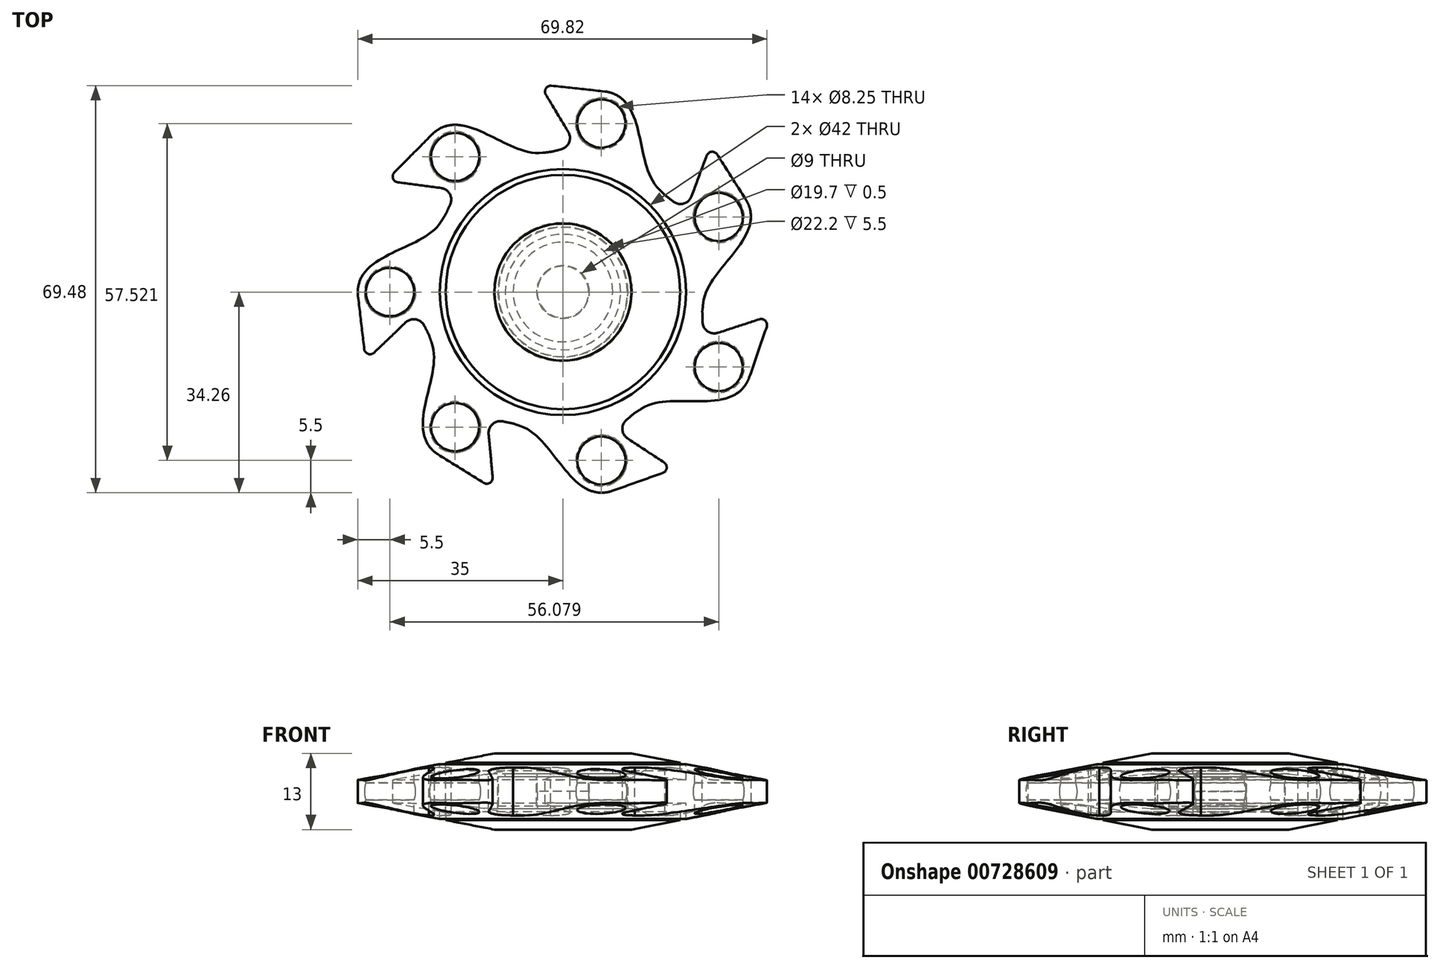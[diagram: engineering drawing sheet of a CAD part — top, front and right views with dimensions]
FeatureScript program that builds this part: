
annotation { "Feature Type Name" : "Feature", "Feature Type Description" : "" }
export const myFeature = defineFeature(function(context is Context, id is Id, definition is map)
    precondition{}
    {
        {
            var Q0;
            Q0=qCreatedBy(makeId("Front.planeOp"),FACE);
            var sketch = newSketch(context, id + "F0", { "sketchPlane" : qUnion([Q0])});
            skLineSegment(sketch, "E0.right", {"start": v(-4.5, -2.5) * mm, "end": v(-4.5, 2.5) * mm});
            skPoint(sketch, "E0.middle", {"position": v(0, 0) * mm});
            skLineSegment(sketch, "E1.right", {"start": v(-20, 6.5) * mm, "end": v(-20, 3.5) * mm});
            skLineSegment(sketch, "E2.right", {"start": v(-8.5, 3) * mm, "end": v(-8.5, 3.5) * mm});
            skLineSegment(sketch, "E3", {"start": v(-8.5, 3.5) * mm, "end": v(-20, 3.5) * mm});
            skLineSegment(sketch, "E4", {"start": v(-11, 2.5) * mm, "end": v(-11, -2.5) * mm});
            skLineSegment(sketch, "E5.top", {"start": v(-4.4, 0) * mm, "end": v(0, 0) * mm});
            skLineSegment(sketch, "E5.left", {"start": v(-4.4, 3) * mm, "end": v(-4.4, 0) * mm});
            skLineSegment(sketch, "E6", {"start": v(-8.5, 3) * mm, "end": v(-4.4, 3) * mm});
            skLineSegment(sketch, "E7", {"start": v(-11, 2.5) * mm, "end": v(-4.5, 2.5) * mm});
            skLineSegment(sketch, "E8", {"start": v(-11, -2.5) * mm, "end": v(-4.5, -2.5) * mm});
            skLineSegment(sketch, "E9", {"start": v(0, 12.94) * mm, "end": v(0, -13.8) * mm});
            skPoint(sketch, "E10.startSnap0", {"position": v(-11, 0) * mm});
            skLineSegment(sketch, "E11.bottom", {"start": v(-21, -5) * mm, "end": v(-24, -5) * mm});
            skLineSegment(sketch, "E11.top", {"start": v(-21, 5) * mm, "end": v(-24, 5) * mm});
            skLineSegment(sketch, "E11.right", {"start": v(-24, -5) * mm, "end": v(-24, 5) * mm});
            skLineSegment(sketch, "E12", {"start": v(-11.1, 2.5) * mm, "end": v(-9.85, 2.5) * mm});
            skLineSegment(sketch, "E13", {"start": v(-9.85, 2.5) * mm, "end": v(-9.85, 3) * mm});
            skLineSegment(sketch, "E14", {"start": v(-9.85, 3) * mm, "end": v(-11.85, 3) * mm});
            skLineSegment(sketch, "E15", {"start": v(-11.85, 3) * mm, "end": v(-21, 2) * mm});
            skLineSegment(sketch, "E16", {"start": v(-11.1, 2.5) * mm, "end": v(-11.1, -3) * mm});
            skLineSegment(sketch, "E17", {"start": v(-21, 2) * mm, "end": v(-21, 5) * mm});
            skLineSegment(sketch, "E18", {"start": v(-21, -2) * mm, "end": v(-21, -5) * mm});
            skLineSegment(sketch, "E19", {"start": v(-11.1, -3) * mm, "end": v(-11.85, -3) * mm});
            skLineSegment(sketch, "E20", {"start": v(-11.85, -3) * mm, "end": v(-21, -2) * mm});
            skLineSegment(sketch, "E21", {"start": v(-20, 6.5) * mm, "end": v(0, 6.5) * mm});
            skLineSegment(sketch, "E22", {"start": v(-4.5, 0) * mm, "end": v(0, 0) * mm});
            skSolve(sketch);
        }
        {
            var Q0;
            {var subQ6=sQuery(id+"F0.wireOp",EDGE,"E4");Q0=makeQuery(id+"F0.imprint","IMPRINT",FACE,{"disambiguationData":[TD([[makeQuery(id+"F0.imprint","IMPRINT",EDGE,{"derivedFrom":subQ6}),1.0]])]});}
            var Q1;
            Q1=sQuery(id+"F0.wireOp",EDGE,"E9");
            revolve(context, id + "F1", {"surfaceOperationType" : NewSurfaceOperationType.NEW, "entities" : qUnion([Q0]), "axis" : qUnion([Q1]), "revolveType" : RevolveType.FULL});
        }
        {
            var Q0;
            Q0=makeQuery(id+"F0.imprint","IMPRINT",FACE,{"disambiguationData":[TD([[makeQuery(id+"F0.imprint","IMPRINT",EDGE,{"derivedFrom":sQuery(id+"F0.wireOp",EDGE,"E1.right")}),1.0]])]});
            var Q1;
            Q1=sQuery(id+"F0.wireOp",EDGE,"E9");
            revolve(context, id + "F2", {"surfaceOperationType" : NewSurfaceOperationType.NEW, "entities" : qUnion([Q0]), "axis" : qUnion([Q1]), "revolveType" : RevolveType.FULL});
        }
        {
            var Q0;
            Q0=makeQuery(id+"F0.imprint","IMPRINT",FACE,{"disambiguationData":[TD([[makeQuery(id+"F0.imprint","IMPRINT",EDGE,{"derivedFrom":sQuery(id+"F0.wireOp",EDGE,"E11.bottom")}),-1.0]])]});
            var Q1;
            Q1=sQuery(id+"F0.wireOp",EDGE,"E9");
            revolve(context, id + "F3", {"surfaceOperationType" : NewSurfaceOperationType.NEW, "entities" : qUnion([Q0]), "axis" : qUnion([Q1]), "revolveType" : RevolveType.FULL});
        }
        {
            var Q0;
            Q0=makeQuery(id+"F3.opRevolve","SWEPT_FACE",FACE,{"disambiguationData":[OSD([sQuery(id+"F0.wireOp",EDGE,"E11.top")])]});
            var sketch = newSketch(context, id + "F4", { "sketchPlane" : qUnion([Q0])});
            skCircle(sketch, "E23", {"center": v(-29.5, 0) * mm, "radius": 5.5 * mm});
            skFitSpline(sketch, "E24", {"points": [v(-20.7, 12.15) * mm, v(-34.9, 1.08) * mm], "startDerivative": vector(-8.4, -14.32) * mm, "endDerivative": vector(-3.5, -17.47) * mm});
            skLineSegment(sketch, "E25", {"start": v(-34.96, -0.64) * mm, "end": v(-33.9, -9.74) * mm});
            skCircle(sketch, "E26", {"center": v(-29.5, 0) * mm, "radius": 4.12 * mm});
            skPoint(sketch, "E27.visualSharp", {"position": v(-33.66, -11.72) * mm});
            skArc(sketch, "E27.filletArc", {"start": v(-33.9, -9.74) * mm, "mid": v(-33.24, -10.57) * mm, "end": v(-32.2, -10.35) * mm});
            skLineSegment(sketch, "E28", {"start": v(-32.2, -10.35) * mm, "end": v(-26.84, -5.2) * mm});
            skLineSegment(sketch, "E29", {"start": v(-23.67, -5.73) * mm, "end": v(-22.85, -7.35) * mm});
            skPoint(sketch, "E30.visualSharp", {"position": v(-24.89, -3.32) * mm});
            skArc(sketch, "E30.filletArc", {"start": v(-23.67, -5.73) * mm, "mid": v(-25.12, -4.66) * mm, "end": v(-26.84, -5.2) * mm});
            skSolve(sketch);
        }
        {
            var Q0;
            {var subQ0=sQuery(id+"F4.wireOp",EDGE,"E24");Q0=makeQuery(id+"F4.imprint","IMPRINT",FACE,{"disambiguationData":[TD([[makeQuery(id+"F4.imprint","IMPRINT",EDGE,{"derivedFrom":subQ0}),1.0]])]});}
            var Q1;
            {var subQ0=sQuery(id+"F4.wireOp",EDGE,"E25");Q1=makeQuery(id+"F4.imprint","IMPRINT",FACE,{"disambiguationData":[TD([[makeQuery(id+"F4.imprint","IMPRINT",EDGE,{"derivedFrom":subQ0}),1.0]])]});}
            var Q2;
            Q2=makeQuery(id+"F4.imprint","IMPRINT",FACE,{"disambiguationData":[TD([[makeQuery(id+"F4.imprint","IMPRINT",EDGE,{"derivedFrom":sQuery(id+"F4.wireOp",EDGE,"E26")}),-1.0]])]});
            var Q3;
            Q3=makeQuery(id+"F3.opRevolve","SWEPT_FACE",FACE,{"disambiguationData":[OSD([sQuery(id+"F0.wireOp",EDGE,"E11.bottom")])]});
            extrude(context, id + "F5", {"entities" : qUnion([Q0, Q1, Q2]), "operationType" : NewBodyOperationType.ADD, "endBound" : BoundingType.UP_TO_SURFACE, "oppositeDirection" : true, "depth" : 25 * mm, "endBoundEntityFace" : qUnion([Q3]), "offsetDistance" : -25 * mm});
        }
        {
            var Q0;
            Q0=makeQuery(id+"F3.opRevolve","SWEPT_BODY",BODY,{"disambiguationData":[OSD([sQuery(id+"F0.wireOp",EDGE,"E7"),sQuery(id+"F0.wireOp",EDGE,"E11.bottom"),sQuery(id+"F0.wireOp",EDGE,"E11.top"),sQuery(id+"F0.wireOp",EDGE,"E11.right"),sQuery(id+"F0.wireOp",EDGE,"E12"),sQuery(id+"F0.wireOp",EDGE,"E13"),sQuery(id+"F0.wireOp",EDGE,"E14"),sQuery(id+"F0.wireOp",EDGE,"E15"),sQuery(id+"F0.wireOp",EDGE,"E16"),sQuery(id+"F0.wireOp",EDGE,"E17"),sQuery(id+"F0.wireOp",EDGE,"E18"),sQuery(id+"F0.wireOp",EDGE,"E19"),sQuery(id+"F0.wireOp",EDGE,"E20")])]});
            var Q1;
            Q1=sQuery(id+"F0.wireOp",EDGE,"E9");
            circularPattern(context, id + "F6", {"operationType" : NewBodyOperationType.ADD, "entities" : qUnion([Q0]), "axis" : qUnion([Q1]), "angle" : 360 * degree, "instanceCount" : 7, "equalSpace" : true});
        }
        {
            var Q0;
            Q0=qCreatedBy(makeId("Front.planeOp"),FACE);
            var sketch = newSketch(context, id + "F7", { "sketchPlane" : qUnion([Q0])});
            skLineSegment(sketch, "E31", {"start": v(0, 18.1) * mm, "end": v(0, -19.67) * mm});
            skLineSegment(sketch, "E32", {"start": v(-4, 8) * mm, "end": v(-45, 0) * mm});
            skLineSegment(sketch, "E33", {"start": v(-45, 0) * mm, "end": v(-4, -8) * mm});
            skLineSegment(sketch, "E34", {"start": v(-4, 8) * mm, "end": v(-45, 8) * mm});
            skLineSegment(sketch, "E35", {"start": v(-45, 8) * mm, "end": v(-45, 0) * mm});
            skLineSegment(sketch, "E36", {"start": v(-45, 0) * mm, "end": v(-45, -8) * mm});
            skLineSegment(sketch, "E37", {"start": v(-45, -8) * mm, "end": v(-4, -8) * mm});
            skSolve(sketch);
        }
        {
            var Q0;
            Q0=makeQuery(id+"F7.imprint","IMPRINT",FACE,{"disambiguationData":[TD([[makeQuery(id+"F7.imprint","IMPRINT",EDGE,{"derivedFrom":sQuery(id+"F7.wireOp",EDGE,"E32")}),-1.0]])]});
            var Q1;
            Q1=makeQuery(id+"F7.imprint","IMPRINT",FACE,{"disambiguationData":[TD([[makeQuery(id+"F7.imprint","IMPRINT",EDGE,{"derivedFrom":sQuery(id+"F7.wireOp",EDGE,"E33")}),-1.0]])]});
            var Q2;
            Q2=sQuery(id+"F7.wireOp",EDGE,"E31");
            revolve(context, id + "F8", {"operationType" : NewBodyOperationType.REMOVE, "surfaceOperationType" : NewSurfaceOperationType.NEW, "entities" : qUnion([Q0, Q1]), "axis" : qUnion([Q2]), "revolveType" : RevolveType.FULL, "oppositeDirection" : true});
        }
        {
            var Q0;
            Q0=makeQuery(id+"F2.opRevolve","SWEPT_BODY",BODY,{"disambiguationData":[OSD([sQuery(id+"F0.wireOp",EDGE,"E1.right"),sQuery(id+"F0.wireOp",EDGE,"E2.right"),sQuery(id+"F0.wireOp",EDGE,"E3"),sQuery(id+"F0.wireOp",EDGE,"E5.top"),sQuery(id+"F0.wireOp",EDGE,"E5.left"),sQuery(id+"F0.wireOp",EDGE,"E6"),sQuery(id+"F0.wireOp",EDGE,"E9"),sQuery(id+"F0.wireOp",EDGE,"E21")])]});
            var Q1;
            Q1=makeQuery(id+"F2.opRevolve","SWEPT_FACE",FACE,{"disambiguationData":[OSD([sQuery(id+"F0.wireOp",EDGE,"E5.top")])]});
            mirror(context, id + "F9", {"entities" : qUnion([Q0]), "mirrorPlane" : qUnion([Q1])});
        }
        {
            var Q0;
            Q0=qCreatedBy(makeId("Top.planeOp"),FACE);
            var sketch = newSketch(context, id + "F10", { "sketchPlane" : qUnion([Q0])});
            skArc(sketch, "E38", {"start": v(-33.87, 0) * mm, "mid": v(-29.5, -4.37) * mm, "end": v(-25.12, 0) * mm});
            skLineSegment(sketch, "E39", {"start": v(-25.12, 0) * mm, "end": v(-33.87, 0) * mm});
            skSolve(sketch);
        }
        {
            var Q0;
            Q0=makeQuery(id+"F10.imprint","IMPRINT",FACE,{"disambiguationData":[TD([[makeQuery(id+"F10.imprint","IMPRINT",EDGE,{"derivedFrom":sQuery(id+"F10.wireOp",EDGE,"E38")}),1.0]])]});
            var Q1;
            Q1=sQuery(id+"F10.wireOp",EDGE,"E39");
            revolve(context, id + "F11", {"surfaceOperationType" : NewSurfaceOperationType.NEW, "entities" : qUnion([Q0]), "axis" : qUnion([Q1]), "revolveType" : RevolveType.FULL, "oppositeDirection" : true});
        }
        {
            var Q0;
            Q0=makeQuery(id+"F11.opRevolve","SWEPT_BODY",BODY,{"disambiguationData":[OSD([sQuery(id+"F10.wireOp",EDGE,"E38"),sQuery(id+"F10.wireOp",EDGE,"E39")])]});
            var Q1;
            Q1=sQuery(id+"F0.wireOp",EDGE,"E9");
            circularPattern(context, id + "F12", {"operationType" : NewBodyOperationType.REMOVE, "entities" : qUnion([Q0]), "axis" : qUnion([Q1]), "angle" : 360 * degree, "instanceCount" : 7, "equalSpace" : true});
        }
    });
